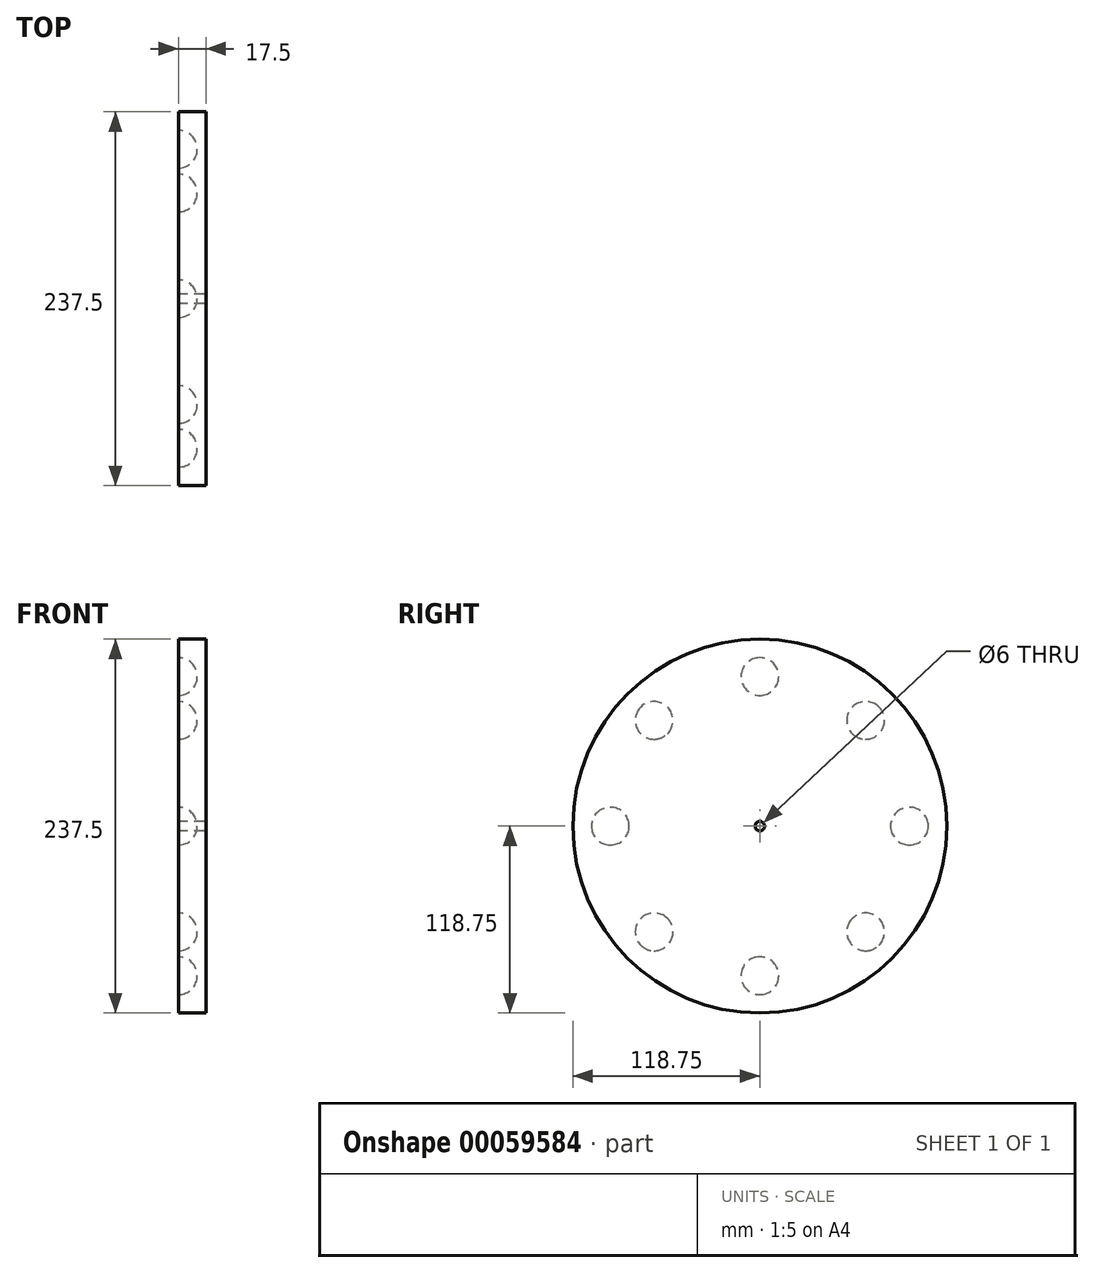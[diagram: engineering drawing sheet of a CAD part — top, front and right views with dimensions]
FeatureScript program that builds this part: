
annotation { "Feature Type Name" : "Feature", "Feature Type Description" : "" }
export const myFeature = defineFeature(function(context is Context, id is Id, definition is map)
    precondition{}
    {
        {
            var Q0;
            Q0=qCreatedBy(makeId("Right.planeOp"),FACE);
            var sketch = newSketch(context, id + "F0", { "sketchPlane" : qUnion([Q0])});
            skCircle(sketch, "E0", {"center": v(0, 0) * mm, "radius": 125 * mm, "construction": true});
            skCircle(sketch, "E1", {"center": v(0, 0) * mm, "radius": 0.81 * mm, "construction": true});
            skLineSegment(sketch, "E2", {"start": v(0, -0.81) * mm, "end": v(0, 0) * mm, "construction": true});
            skLineSegment(sketch, "E3", {"start": v(0, 0.81) * mm, "end": v(0, -0.81) * mm});
            skLineSegment(sketch, "E4", {"start": v(0, -0.81) * mm, "end": v(-5.3, 118.63) * mm});
            skLineSegment(sketch, "E5.MirrorCS", {"start": v(0, -0.81) * mm, "end": v(0, 0.81) * mm});
            skLineSegment(sketch, "E6.MirrorCS", {"start": v(0, -0.81) * mm, "end": v(5.3, 118.63) * mm});
            skCircle(sketch, "E7", {"center": v(0, 0) * mm, "radius": 118.75 * mm, "construction": true});
            skCircle(sketch, "E8", {"center": v(0, 0) * mm, "radius": 118.75 * mm});
            skLineSegment(sketch, "E9.1.0", {"start": v(0.1, -0.8) * mm, "end": v(-9.61, 118.36) * mm});
            skLineSegment(sketch, "E9.1.1", {"start": v(0.1, -0.8) * mm, "end": v(-20.13, 117.03) * mm});
            skLineSegment(sketch, "E9.1.2", {"start": v(-0.1, 0.8) * mm, "end": v(0.1, -0.8) * mm});
            skLineSegment(sketch, "E9.1.3", {"start": v(0.1, -0.8) * mm, "end": v(-0.1, 0.8) * mm});
            skLineSegment(sketch, "E9.2.0", {"start": v(0.2, -0.79) * mm, "end": v(-24.37, 116.22) * mm});
            skLineSegment(sketch, "E9.2.1", {"start": v(0.2, -0.79) * mm, "end": v(-34.64, 113.59) * mm});
            skLineSegment(sketch, "E9.2.2", {"start": v(-0.2, 0.79) * mm, "end": v(0.2, -0.79) * mm});
            skLineSegment(sketch, "E9.2.3", {"start": v(0.2, -0.79) * mm, "end": v(-0.2, 0.79) * mm});
            skLineSegment(sketch, "E10.3.3.0", {"start": v(0.3, -0.76) * mm, "end": v(-48.6, 108.35) * mm});
            skLineSegment(sketch, "E10.5.3.0", {"start": v(0.3, -0.76) * mm, "end": v(-38.74, 112.25) * mm});
            skLineSegment(sketch, "E10.6.3.0", {"start": v(-0.3, 0.76) * mm, "end": v(0.3, -0.76) * mm});
            skLineSegment(sketch, "E10.9.3.0", {"start": v(0.3, -0.76) * mm, "end": v(-0.3, 0.76) * mm});
            skLineSegment(sketch, "E10.3.4.0", {"start": v(0.4, -0.71) * mm, "end": v(-61.8, 101.4) * mm});
            skLineSegment(sketch, "E10.5.4.0", {"start": v(0.4, -0.71) * mm, "end": v(-52.5, 106.51) * mm});
            skLineSegment(sketch, "E10.6.4.0", {"start": v(-0.4, 0.71) * mm, "end": v(0.4, -0.71) * mm});
            skLineSegment(sketch, "E10.9.4.0", {"start": v(0.4, -0.71) * mm, "end": v(-0.4, 0.71) * mm});
            skLineSegment(sketch, "E10.3.5.0", {"start": v(0.48, -0.66) * mm, "end": v(-74.02, 92.86) * mm});
            skLineSegment(sketch, "E10.5.5.0", {"start": v(0.48, -0.66) * mm, "end": v(-65.44, 99.1) * mm});
            skLineSegment(sketch, "E10.6.5.0", {"start": v(-0.48, 0.66) * mm, "end": v(0.48, -0.66) * mm});
            skLineSegment(sketch, "E10.9.5.0", {"start": v(0.48, -0.66) * mm, "end": v(-0.48, 0.66) * mm});
            skLineSegment(sketch, "E10.3.6.0", {"start": v(0.56, -0.6) * mm, "end": v(-85.07, 82.85) * mm});
            skLineSegment(sketch, "E10.5.6.0", {"start": v(0.56, -0.6) * mm, "end": v(-77.35, 90.1) * mm});
            skLineSegment(sketch, "E10.6.6.0", {"start": v(-0.56, 0.6) * mm, "end": v(0.56, -0.6) * mm});
            skLineSegment(sketch, "E10.9.6.0", {"start": v(0.56, -0.6) * mm, "end": v(-0.56, 0.6) * mm});
            skLineSegment(sketch, "E10.3.7.0", {"start": v(0.63, -0.52) * mm, "end": v(-94.79, 71.53) * mm});
            skLineSegment(sketch, "E10.5.7.0", {"start": v(0.63, -0.52) * mm, "end": v(-88.03, 79.7) * mm});
            skLineSegment(sketch, "E10.6.7.0", {"start": v(-0.63, 0.52) * mm, "end": v(0.63, -0.52) * mm});
            skLineSegment(sketch, "E10.9.7.0", {"start": v(0.63, -0.52) * mm, "end": v(-0.63, 0.52) * mm});
            skLineSegment(sketch, "E10.3.8.0", {"start": v(0.69, -0.44) * mm, "end": v(-103, 59.1) * mm});
            skLineSegment(sketch, "E10.5.8.0", {"start": v(0.69, -0.44) * mm, "end": v(-97.32, 68.04) * mm});
            skLineSegment(sketch, "E10.6.8.0", {"start": v(-0.69, 0.44) * mm, "end": v(0.69, -0.44) * mm});
            skLineSegment(sketch, "E10.9.8.0", {"start": v(0.69, -0.44) * mm, "end": v(-0.69, 0.44) * mm});
            skLineSegment(sketch, "E10.3.9.0", {"start": v(0.74, -0.35) * mm, "end": v(-109.6, 45.72) * mm});
            skLineSegment(sketch, "E10.5.9.0", {"start": v(0.74, -0.35) * mm, "end": v(-105.08, 55.3) * mm});
            skLineSegment(sketch, "E10.6.9.0", {"start": v(-0.74, 0.35) * mm, "end": v(0.74, -0.35) * mm});
            skLineSegment(sketch, "E10.9.9.0", {"start": v(0.74, -0.35) * mm, "end": v(-0.74, 0.35) * mm});
            skLineSegment(sketch, "E10.3.10.0", {"start": v(0.77, -0.25) * mm, "end": v(-114.46, 31.62) * mm});
            skLineSegment(sketch, "E10.5.10.0", {"start": v(0.77, -0.25) * mm, "end": v(-111.19, 41.7) * mm});
            skLineSegment(sketch, "E10.6.10.0", {"start": v(-0.77, 0.25) * mm, "end": v(0.77, -0.25) * mm});
            skLineSegment(sketch, "E10.9.10.0", {"start": v(0.77, -0.25) * mm, "end": v(-0.77, 0.25) * mm});
            skLineSegment(sketch, "E10.3.11.0", {"start": v(0.8, -0.15) * mm, "end": v(-117.52, 17.02) * mm});
            skLineSegment(sketch, "E10.5.11.0", {"start": v(0.8, -0.15) * mm, "end": v(-115.54, 27.44) * mm});
            skLineSegment(sketch, "E10.6.11.0", {"start": v(-0.8, 0.15) * mm, "end": v(0.8, -0.15) * mm});
            skLineSegment(sketch, "E10.9.11.0", {"start": v(0.8, -0.15) * mm, "end": v(-0.8, 0.15) * mm});
            skLineSegment(sketch, "E10.3.12.0", {"start": v(0.81, -0.05) * mm, "end": v(-118.73, 2.16) * mm});
            skLineSegment(sketch, "E10.5.12.0", {"start": v(0.81, -0.05) * mm, "end": v(-118.06, 12.74) * mm});
            skLineSegment(sketch, "E10.6.12.0", {"start": v(-0.81, 0.05) * mm, "end": v(0.81, -0.05) * mm});
            skLineSegment(sketch, "E10.9.12.0", {"start": v(0.81, -0.05) * mm, "end": v(-0.81, 0.05) * mm});
            skLineSegment(sketch, "E10.3.13.0", {"start": v(0.81, 0.05) * mm, "end": v(-118.06, -12.74) * mm});
            skLineSegment(sketch, "E10.5.13.0", {"start": v(0.81, 0.05) * mm, "end": v(-118.73, -2.16) * mm});
            skLineSegment(sketch, "E10.6.13.0", {"start": v(-0.81, -0.05) * mm, "end": v(0.81, 0.05) * mm});
            skLineSegment(sketch, "E10.9.13.0", {"start": v(0.81, 0.05) * mm, "end": v(-0.81, -0.05) * mm});
            skLineSegment(sketch, "E10.3.14.0", {"start": v(0.8, 0.15) * mm, "end": v(-115.54, -27.44) * mm});
            skLineSegment(sketch, "E10.5.14.0", {"start": v(0.8, 0.15) * mm, "end": v(-117.52, -17.02) * mm});
            skLineSegment(sketch, "E10.6.14.0", {"start": v(-0.8, -0.15) * mm, "end": v(0.8, 0.15) * mm});
            skLineSegment(sketch, "E10.9.14.0", {"start": v(0.8, 0.15) * mm, "end": v(-0.8, -0.15) * mm});
            skLineSegment(sketch, "E10.3.15.0", {"start": v(0.77, 0.25) * mm, "end": v(-111.19, -41.7) * mm});
            skLineSegment(sketch, "E10.5.15.0", {"start": v(0.77, 0.25) * mm, "end": v(-114.46, -31.62) * mm});
            skLineSegment(sketch, "E10.6.15.0", {"start": v(-0.77, -0.25) * mm, "end": v(0.77, 0.25) * mm});
            skLineSegment(sketch, "E10.9.15.0", {"start": v(0.77, 0.25) * mm, "end": v(-0.77, -0.25) * mm});
            skLineSegment(sketch, "E10.3.16.0", {"start": v(0.74, 0.35) * mm, "end": v(-105.08, -55.3) * mm});
            skLineSegment(sketch, "E10.5.16.0", {"start": v(0.74, 0.35) * mm, "end": v(-109.6, -45.72) * mm});
            skLineSegment(sketch, "E10.6.16.0", {"start": v(-0.74, -0.35) * mm, "end": v(0.74, 0.35) * mm});
            skLineSegment(sketch, "E10.9.16.0", {"start": v(0.74, 0.35) * mm, "end": v(-0.74, -0.35) * mm});
            skLineSegment(sketch, "E10.3.17.0", {"start": v(0.69, 0.44) * mm, "end": v(-97.32, -68.04) * mm});
            skLineSegment(sketch, "E10.5.17.0", {"start": v(0.69, 0.44) * mm, "end": v(-103, -59.1) * mm});
            skLineSegment(sketch, "E10.6.17.0", {"start": v(-0.69, -0.44) * mm, "end": v(0.69, 0.44) * mm});
            skLineSegment(sketch, "E10.9.17.0", {"start": v(0.69, 0.44) * mm, "end": v(-0.69, -0.44) * mm});
            skLineSegment(sketch, "E10.3.18.0", {"start": v(0.63, 0.52) * mm, "end": v(-88.03, -79.7) * mm});
            skLineSegment(sketch, "E10.5.18.0", {"start": v(0.63, 0.52) * mm, "end": v(-94.79, -71.53) * mm});
            skLineSegment(sketch, "E10.6.18.0", {"start": v(-0.63, -0.52) * mm, "end": v(0.63, 0.52) * mm});
            skLineSegment(sketch, "E10.9.18.0", {"start": v(0.63, 0.52) * mm, "end": v(-0.63, -0.52) * mm});
            skLineSegment(sketch, "E10.3.19.0", {"start": v(0.56, 0.6) * mm, "end": v(-77.35, -90.1) * mm});
            skLineSegment(sketch, "E10.5.19.0", {"start": v(0.56, 0.6) * mm, "end": v(-85.07, -82.85) * mm});
            skLineSegment(sketch, "E10.6.19.0", {"start": v(-0.56, -0.6) * mm, "end": v(0.56, 0.6) * mm});
            skLineSegment(sketch, "E10.9.19.0", {"start": v(0.56, 0.6) * mm, "end": v(-0.56, -0.6) * mm});
            skLineSegment(sketch, "E10.3.20.0", {"start": v(0.48, 0.66) * mm, "end": v(-65.44, -99.1) * mm});
            skLineSegment(sketch, "E10.5.20.0", {"start": v(0.48, 0.66) * mm, "end": v(-74.02, -92.86) * mm});
            skLineSegment(sketch, "E10.6.20.0", {"start": v(-0.48, -0.66) * mm, "end": v(0.48, 0.66) * mm});
            skLineSegment(sketch, "E10.9.20.0", {"start": v(0.48, 0.66) * mm, "end": v(-0.48, -0.66) * mm});
            skLineSegment(sketch, "E10.3.21.0", {"start": v(0.4, 0.71) * mm, "end": v(-52.5, -106.51) * mm});
            skLineSegment(sketch, "E10.5.21.0", {"start": v(0.4, 0.71) * mm, "end": v(-61.8, -101.4) * mm});
            skLineSegment(sketch, "E10.6.21.0", {"start": v(-0.4, -0.71) * mm, "end": v(0.4, 0.71) * mm});
            skLineSegment(sketch, "E10.9.21.0", {"start": v(0.4, 0.71) * mm, "end": v(-0.4, -0.71) * mm});
            skLineSegment(sketch, "E10.3.22.0", {"start": v(0.3, 0.76) * mm, "end": v(-38.74, -112.25) * mm});
            skLineSegment(sketch, "E10.5.22.0", {"start": v(0.3, 0.76) * mm, "end": v(-48.6, -108.35) * mm});
            skLineSegment(sketch, "E10.6.22.0", {"start": v(-0.3, -0.76) * mm, "end": v(0.3, 0.76) * mm});
            skLineSegment(sketch, "E10.9.22.0", {"start": v(0.3, 0.76) * mm, "end": v(-0.3, -0.76) * mm});
            skLineSegment(sketch, "E10.3.23.0", {"start": v(0.2, 0.79) * mm, "end": v(-24.37, -116.22) * mm});
            skLineSegment(sketch, "E10.5.23.0", {"start": v(0.2, 0.79) * mm, "end": v(-34.64, -113.59) * mm});
            skLineSegment(sketch, "E10.6.23.0", {"start": v(-0.2, -0.79) * mm, "end": v(0.2, 0.79) * mm});
            skLineSegment(sketch, "E10.9.23.0", {"start": v(0.2, 0.79) * mm, "end": v(-0.2, -0.79) * mm});
            skLineSegment(sketch, "E10.3.24.0", {"start": v(0.1, 0.8) * mm, "end": v(-9.61, -118.36) * mm});
            skLineSegment(sketch, "E10.5.24.0", {"start": v(0.1, 0.8) * mm, "end": v(-20.13, -117.03) * mm});
            skLineSegment(sketch, "E10.6.24.0", {"start": v(-0.1, -0.8) * mm, "end": v(0.1, 0.8) * mm});
            skLineSegment(sketch, "E10.9.24.0", {"start": v(0.1, 0.8) * mm, "end": v(-0.1, -0.8) * mm});
            skLineSegment(sketch, "E10.3.25.0", {"start": v(0, 0.81) * mm, "end": v(5.3, -118.63) * mm});
            skLineSegment(sketch, "E10.5.25.0", {"start": v(0, 0.81) * mm, "end": v(-5.3, -118.63) * mm});
            skLineSegment(sketch, "E10.3.26.0", {"start": v(-0.1, 0.8) * mm, "end": v(20.13, -117.03) * mm});
            skLineSegment(sketch, "E10.5.26.0", {"start": v(-0.1, 0.8) * mm, "end": v(9.61, -118.36) * mm});
            skLineSegment(sketch, "E10.3.27.0", {"start": v(-0.2, 0.79) * mm, "end": v(34.64, -113.59) * mm});
            skLineSegment(sketch, "E10.5.27.0", {"start": v(-0.2, 0.79) * mm, "end": v(24.37, -116.22) * mm});
            skLineSegment(sketch, "E10.3.28.0", {"start": v(-0.3, 0.76) * mm, "end": v(48.6, -108.35) * mm});
            skLineSegment(sketch, "E10.5.28.0", {"start": v(-0.3, 0.76) * mm, "end": v(38.74, -112.25) * mm});
            skLineSegment(sketch, "E10.6.28.0", {"start": v(0.3, -0.76) * mm, "end": v(-0.3, 0.76) * mm});
            skLineSegment(sketch, "E10.9.28.0", {"start": v(-0.3, 0.76) * mm, "end": v(0.3, -0.76) * mm});
            skLineSegment(sketch, "E10.3.29.0", {"start": v(-0.4, 0.71) * mm, "end": v(61.8, -101.4) * mm});
            skLineSegment(sketch, "E10.5.29.0", {"start": v(-0.4, 0.71) * mm, "end": v(52.5, -106.51) * mm});
            skLineSegment(sketch, "E10.6.29.0", {"start": v(0.4, -0.71) * mm, "end": v(-0.4, 0.71) * mm});
            skLineSegment(sketch, "E10.9.29.0", {"start": v(-0.4, 0.71) * mm, "end": v(0.4, -0.71) * mm});
            skLineSegment(sketch, "E10.3.30.0", {"start": v(-0.48, 0.66) * mm, "end": v(74.02, -92.86) * mm});
            skLineSegment(sketch, "E10.5.30.0", {"start": v(-0.48, 0.66) * mm, "end": v(65.44, -99.1) * mm});
            skLineSegment(sketch, "E10.6.30.0", {"start": v(0.48, -0.66) * mm, "end": v(-0.48, 0.66) * mm});
            skLineSegment(sketch, "E10.9.30.0", {"start": v(-0.48, 0.66) * mm, "end": v(0.48, -0.66) * mm});
            skLineSegment(sketch, "E10.3.31.0", {"start": v(-0.56, 0.6) * mm, "end": v(85.07, -82.85) * mm});
            skLineSegment(sketch, "E10.5.31.0", {"start": v(-0.56, 0.6) * mm, "end": v(77.35, -90.1) * mm});
            skLineSegment(sketch, "E10.6.31.0", {"start": v(0.56, -0.6) * mm, "end": v(-0.56, 0.6) * mm});
            skLineSegment(sketch, "E10.9.31.0", {"start": v(-0.56, 0.6) * mm, "end": v(0.56, -0.6) * mm});
            skLineSegment(sketch, "E10.3.32.0", {"start": v(-0.63, 0.52) * mm, "end": v(94.79, -71.53) * mm});
            skLineSegment(sketch, "E10.5.32.0", {"start": v(-0.63, 0.52) * mm, "end": v(88.03, -79.7) * mm});
            skLineSegment(sketch, "E10.6.32.0", {"start": v(0.63, -0.52) * mm, "end": v(-0.63, 0.52) * mm});
            skLineSegment(sketch, "E10.9.32.0", {"start": v(-0.63, 0.52) * mm, "end": v(0.63, -0.52) * mm});
            skLineSegment(sketch, "E10.3.33.0", {"start": v(-0.69, 0.44) * mm, "end": v(103, -59.1) * mm});
            skLineSegment(sketch, "E10.5.33.0", {"start": v(-0.69, 0.44) * mm, "end": v(97.32, -68.04) * mm});
            skLineSegment(sketch, "E10.6.33.0", {"start": v(0.69, -0.44) * mm, "end": v(-0.69, 0.44) * mm});
            skLineSegment(sketch, "E10.9.33.0", {"start": v(-0.69, 0.44) * mm, "end": v(0.69, -0.44) * mm});
            skLineSegment(sketch, "E10.3.34.0", {"start": v(-0.74, 0.35) * mm, "end": v(109.6, -45.72) * mm});
            skLineSegment(sketch, "E10.5.34.0", {"start": v(-0.74, 0.35) * mm, "end": v(105.08, -55.3) * mm});
            skLineSegment(sketch, "E10.6.34.0", {"start": v(0.74, -0.35) * mm, "end": v(-0.74, 0.35) * mm});
            skLineSegment(sketch, "E10.9.34.0", {"start": v(-0.74, 0.35) * mm, "end": v(0.74, -0.35) * mm});
            skLineSegment(sketch, "E10.3.35.0", {"start": v(-0.77, 0.25) * mm, "end": v(114.46, -31.62) * mm});
            skLineSegment(sketch, "E10.5.35.0", {"start": v(-0.77, 0.25) * mm, "end": v(111.19, -41.7) * mm});
            skLineSegment(sketch, "E10.6.35.0", {"start": v(0.77, -0.25) * mm, "end": v(-0.77, 0.25) * mm});
            skLineSegment(sketch, "E10.9.35.0", {"start": v(-0.77, 0.25) * mm, "end": v(0.77, -0.25) * mm});
            skLineSegment(sketch, "E10.3.36.0", {"start": v(-0.8, 0.15) * mm, "end": v(117.52, -17.02) * mm});
            skLineSegment(sketch, "E10.5.36.0", {"start": v(-0.8, 0.15) * mm, "end": v(115.54, -27.44) * mm});
            skLineSegment(sketch, "E10.6.36.0", {"start": v(0.8, -0.15) * mm, "end": v(-0.8, 0.15) * mm});
            skLineSegment(sketch, "E10.9.36.0", {"start": v(-0.8, 0.15) * mm, "end": v(0.8, -0.15) * mm});
            skLineSegment(sketch, "E10.3.37.0", {"start": v(-0.81, 0.05) * mm, "end": v(118.73, -2.16) * mm});
            skLineSegment(sketch, "E10.5.37.0", {"start": v(-0.81, 0.05) * mm, "end": v(118.06, -12.74) * mm});
            skLineSegment(sketch, "E10.6.37.0", {"start": v(0.81, -0.05) * mm, "end": v(-0.81, 0.05) * mm});
            skLineSegment(sketch, "E10.9.37.0", {"start": v(-0.81, 0.05) * mm, "end": v(0.81, -0.05) * mm});
            skLineSegment(sketch, "E10.3.38.0", {"start": v(-0.81, -0.05) * mm, "end": v(118.06, 12.74) * mm});
            skLineSegment(sketch, "E10.5.38.0", {"start": v(-0.81, -0.05) * mm, "end": v(118.73, 2.16) * mm});
            skLineSegment(sketch, "E10.6.38.0", {"start": v(0.81, 0.05) * mm, "end": v(-0.81, -0.05) * mm});
            skLineSegment(sketch, "E10.9.38.0", {"start": v(-0.81, -0.05) * mm, "end": v(0.81, 0.05) * mm});
            skLineSegment(sketch, "E10.3.39.0", {"start": v(-0.8, -0.15) * mm, "end": v(115.54, 27.44) * mm});
            skLineSegment(sketch, "E10.5.39.0", {"start": v(-0.8, -0.15) * mm, "end": v(117.52, 17.02) * mm});
            skLineSegment(sketch, "E10.6.39.0", {"start": v(0.8, 0.15) * mm, "end": v(-0.8, -0.15) * mm});
            skLineSegment(sketch, "E10.9.39.0", {"start": v(-0.8, -0.15) * mm, "end": v(0.8, 0.15) * mm});
            skLineSegment(sketch, "E10.3.40.0", {"start": v(-0.77, -0.25) * mm, "end": v(111.19, 41.7) * mm});
            skLineSegment(sketch, "E10.5.40.0", {"start": v(-0.77, -0.25) * mm, "end": v(114.46, 31.62) * mm});
            skLineSegment(sketch, "E10.6.40.0", {"start": v(0.77, 0.25) * mm, "end": v(-0.77, -0.25) * mm});
            skLineSegment(sketch, "E10.9.40.0", {"start": v(-0.77, -0.25) * mm, "end": v(0.77, 0.25) * mm});
            skLineSegment(sketch, "E10.3.41.0", {"start": v(-0.74, -0.35) * mm, "end": v(105.08, 55.3) * mm});
            skLineSegment(sketch, "E10.5.41.0", {"start": v(-0.74, -0.35) * mm, "end": v(109.6, 45.72) * mm});
            skLineSegment(sketch, "E10.6.41.0", {"start": v(0.74, 0.35) * mm, "end": v(-0.74, -0.35) * mm});
            skLineSegment(sketch, "E10.9.41.0", {"start": v(-0.74, -0.35) * mm, "end": v(0.74, 0.35) * mm});
            skLineSegment(sketch, "E10.3.42.0", {"start": v(-0.69, -0.44) * mm, "end": v(97.32, 68.04) * mm});
            skLineSegment(sketch, "E10.5.42.0", {"start": v(-0.69, -0.44) * mm, "end": v(103, 59.1) * mm});
            skLineSegment(sketch, "E10.6.42.0", {"start": v(0.69, 0.44) * mm, "end": v(-0.69, -0.44) * mm});
            skLineSegment(sketch, "E10.9.42.0", {"start": v(-0.69, -0.44) * mm, "end": v(0.69, 0.44) * mm});
            skLineSegment(sketch, "E10.3.43.0", {"start": v(-0.63, -0.52) * mm, "end": v(88.03, 79.7) * mm});
            skLineSegment(sketch, "E10.5.43.0", {"start": v(-0.63, -0.52) * mm, "end": v(94.79, 71.53) * mm});
            skLineSegment(sketch, "E10.6.43.0", {"start": v(0.63, 0.52) * mm, "end": v(-0.63, -0.52) * mm});
            skLineSegment(sketch, "E10.9.43.0", {"start": v(-0.63, -0.52) * mm, "end": v(0.63, 0.52) * mm});
            skLineSegment(sketch, "E10.3.44.0", {"start": v(-0.56, -0.6) * mm, "end": v(77.35, 90.1) * mm});
            skLineSegment(sketch, "E10.5.44.0", {"start": v(-0.56, -0.6) * mm, "end": v(85.07, 82.85) * mm});
            skLineSegment(sketch, "E10.6.44.0", {"start": v(0.56, 0.6) * mm, "end": v(-0.56, -0.6) * mm});
            skLineSegment(sketch, "E10.9.44.0", {"start": v(-0.56, -0.6) * mm, "end": v(0.56, 0.6) * mm});
            skLineSegment(sketch, "E10.3.45.0", {"start": v(-0.48, -0.66) * mm, "end": v(65.44, 99.1) * mm});
            skLineSegment(sketch, "E10.5.45.0", {"start": v(-0.48, -0.66) * mm, "end": v(74.02, 92.86) * mm});
            skLineSegment(sketch, "E10.6.45.0", {"start": v(0.48, 0.66) * mm, "end": v(-0.48, -0.66) * mm});
            skLineSegment(sketch, "E10.9.45.0", {"start": v(-0.48, -0.66) * mm, "end": v(0.48, 0.66) * mm});
            skLineSegment(sketch, "E10.3.46.0", {"start": v(-0.4, -0.71) * mm, "end": v(52.5, 106.51) * mm});
            skLineSegment(sketch, "E10.5.46.0", {"start": v(-0.4, -0.71) * mm, "end": v(61.8, 101.4) * mm});
            skLineSegment(sketch, "E10.6.46.0", {"start": v(0.4, 0.71) * mm, "end": v(-0.4, -0.71) * mm});
            skLineSegment(sketch, "E10.9.46.0", {"start": v(-0.4, -0.71) * mm, "end": v(0.4, 0.71) * mm});
            skLineSegment(sketch, "E10.3.47.0", {"start": v(-0.3, -0.76) * mm, "end": v(38.74, 112.25) * mm});
            skLineSegment(sketch, "E10.5.47.0", {"start": v(-0.3, -0.76) * mm, "end": v(48.6, 108.35) * mm});
            skLineSegment(sketch, "E10.6.47.0", {"start": v(0.3, 0.76) * mm, "end": v(-0.3, -0.76) * mm});
            skLineSegment(sketch, "E10.9.47.0", {"start": v(-0.3, -0.76) * mm, "end": v(0.3, 0.76) * mm});
            skLineSegment(sketch, "E10.3.48.0", {"start": v(-0.2, -0.79) * mm, "end": v(24.37, 116.22) * mm});
            skLineSegment(sketch, "E10.5.48.0", {"start": v(-0.2, -0.79) * mm, "end": v(34.64, 113.59) * mm});
            skLineSegment(sketch, "E10.6.48.0", {"start": v(0.2, 0.79) * mm, "end": v(-0.2, -0.79) * mm});
            skLineSegment(sketch, "E10.9.48.0", {"start": v(-0.2, -0.79) * mm, "end": v(0.2, 0.79) * mm});
            skLineSegment(sketch, "E10.3.49.0", {"start": v(-0.1, -0.8) * mm, "end": v(9.61, 118.36) * mm});
            skLineSegment(sketch, "E10.5.49.0", {"start": v(-0.1, -0.8) * mm, "end": v(20.13, 117.03) * mm});
            skLineSegment(sketch, "E10.6.49.0", {"start": v(0.1, 0.8) * mm, "end": v(-0.1, -0.8) * mm});
            skLineSegment(sketch, "E10.9.49.0", {"start": v(-0.1, -0.8) * mm, "end": v(0.1, 0.8) * mm});
            skSolve(sketch);
        }
        {
            var Q0;
            Q0 = qSketchRegion(id + "F0", true);
            extrude(context, id + "F1", {"entities" : qUnion([Q0]), "depth" : 17.5 * mm});
        }
        {
            var Q0;
            Q0=makeQuery(id+"Fn8MloqXUjJoPmc_1.boolean.opBoolean","MERGE",FACE,{"derivedFrom":[makeQuery(id+"F1.opExtrude","CAP_FACE",FACE,{"disambiguationData":[OSD([sQuery(id+"F0.wireOp",EDGE,"E3"),sQuery(id+"F0.wireOp",EDGE,"E4"),sQuery(id+"F0.wireOp",EDGE,"E5.MirrorCS"),sQuery(id+"F0.wireOp",EDGE,"E6.MirrorCS"),sQuery(id+"F0.wireOp",EDGE,"OQRqwsvV-qcOx-RosJ-7bpL-tB40Y6nJSxaw"),sQuery(id+"F0.wireOp",EDGE,"t5HJLBER-EOSb-2UTf-ySmI-mLM6b4EdJLG6"),sQuery(id+"F0.wireOp",EDGE,"OaBUUnl9-dybp-6rTC-3uGv-TSD4vVyGhlnP")])],"isStart":true}),makeQuery(id+"Fn8MloqXUjJoPmc_1.opExtrude","CAP_FACE",FACE,{"disambiguationData":[OSD([sQuery(id+"Fj8ZmPuuntyTscv_1.wireOp",EDGE,"wY98nEZC-u4MA-k90t-BY2E-VeJdUgsrrei2")])],"isStart":true})]});
            var sketch = newSketch(context, id + "F2", { "sketchPlane" : qUnion([Q0])});
            skArc(sketch, "E11", {"start": v(0, 83) * mm, "mid": v(12, 95) * mm, "end": v(0, 107) * mm});
            skLineSegment(sketch, "E12", {"start": v(0, 83) * mm, "end": v(0, 107) * mm});
            skSolve(sketch);
        }
        {
            var Q0;
            Q0 = qSketchRegion(id + "F2", true);
            var Q1;
            Q1=sQuery(id+"F2.wireOp",EDGE,"E12");
            revolve(context, id + "F3", {"operationType" : NewBodyOperationType.REMOVE, "entities" : qUnion([Q0]), "axis" : qUnion([Q1]), "revolveType" : RevolveType.ONE_DIRECTION, "angle" : 180 * degree});
        }
        {
            var Q0;
            Q0=makeQuery(id+"Fn8MloqXUjJoPmc_1.boolean.opBoolean","MERGE",FACE,{"derivedFrom":[makeQuery(id+"F1.opExtrude","CAP_FACE",FACE,{"disambiguationData":[OSD([sQuery(id+"F0.wireOp",EDGE,"E3"),sQuery(id+"F0.wireOp",EDGE,"E4"),sQuery(id+"F0.wireOp",EDGE,"E5.MirrorCS"),sQuery(id+"F0.wireOp",EDGE,"E6.MirrorCS"),sQuery(id+"F0.wireOp",EDGE,"OQRqwsvV-qcOx-RosJ-7bpL-tB40Y6nJSxaw"),sQuery(id+"F0.wireOp",EDGE,"t5HJLBER-EOSb-2UTf-ySmI-mLM6b4EdJLG6"),sQuery(id+"F0.wireOp",EDGE,"OaBUUnl9-dybp-6rTC-3uGv-TSD4vVyGhlnP")])],"isStart":true}),makeQuery(id+"Fn8MloqXUjJoPmc_1.opExtrude","CAP_FACE",FACE,{"disambiguationData":[OSD([sQuery(id+"Fj8ZmPuuntyTscv_1.wireOp",EDGE,"wY98nEZC-u4MA-k90t-BY2E-VeJdUgsrrei2")])],"isStart":true})]});
            var sketch = newSketch(context, id + "F4", { "sketchPlane" : qUnion([Q0])});
            skArc(sketch, "E13", {"start": v(58.69, 58.69) * mm, "mid": v(75.66, 58.69) * mm, "end": v(75.66, 75.66) * mm});
            skLineSegment(sketch, "E14", {"start": v(0, 0) * mm, "end": v(67.18, 67.18) * mm, "construction": true});
            skLineSegment(sketch, "E15", {"start": v(58.69, 58.69) * mm, "end": v(75.66, 75.66) * mm});
            skSolve(sketch);
        }
        {
            var Q0;
            Q0=makeQuery(id+"F4.imprint","IMPRINT",FACE,{"disambiguationData":[TD([[makeQuery(id+"F4.imprint","IMPRINT",EDGE,{"derivedFrom":sQuery(id+"F4.wireOp",EDGE,"E13")}),1.0]])]});
            var Q1;
            Q1=sQuery(id+"F4.wireOp",EDGE,"E14");
            revolve(context, id + "F5", {"operationType" : NewBodyOperationType.REMOVE, "entities" : qUnion([Q0]), "axis" : qUnion([Q1]), "revolveType" : RevolveType.FULL, "oppositeDirection" : true});
        }
        {
            var Q0;
            Q0=makeQuery(id+"Fn8MloqXUjJoPmc_1.boolean.opBoolean","MERGE",FACE,{"derivedFrom":[makeQuery(id+"F1.opExtrude","CAP_FACE",FACE,{"disambiguationData":[OSD([sQuery(id+"F0.wireOp",EDGE,"E3"),sQuery(id+"F0.wireOp",EDGE,"E4"),sQuery(id+"F0.wireOp",EDGE,"E5.MirrorCS"),sQuery(id+"F0.wireOp",EDGE,"E6.MirrorCS"),sQuery(id+"F0.wireOp",EDGE,"OQRqwsvV-qcOx-RosJ-7bpL-tB40Y6nJSxaw"),sQuery(id+"F0.wireOp",EDGE,"t5HJLBER-EOSb-2UTf-ySmI-mLM6b4EdJLG6"),sQuery(id+"F0.wireOp",EDGE,"OaBUUnl9-dybp-6rTC-3uGv-TSD4vVyGhlnP")])],"isStart":true}),makeQuery(id+"Fn8MloqXUjJoPmc_1.opExtrude","CAP_FACE",FACE,{"disambiguationData":[OSD([sQuery(id+"Fj8ZmPuuntyTscv_1.wireOp",EDGE,"wY98nEZC-u4MA-k90t-BY2E-VeJdUgsrrei2")])],"isStart":true})]});
            var sketch = newSketch(context, id + "F6", { "sketchPlane" : qUnion([Q0])});
            skLineSegment(sketch, "E16", {"start": v(0, 0) * mm, "end": v(95, 0) * mm, "construction": true});
            skArc(sketch, "E17", {"start": v(83, 0) * mm, "mid": v(95, -12) * mm, "end": v(107, 0) * mm});
            skLineSegment(sketch, "E18", {"start": v(83, 0) * mm, "end": v(107, 0) * mm});
            skSolve(sketch);
        }
        {
            var Q0;
            Q0 = qSketchRegion(id + "F6", true);
            var Q1;
            Q1=sQuery(id+"F6.wireOp",EDGE,"E16");
            revolve(context, id + "F7", {"operationType" : NewBodyOperationType.REMOVE, "entities" : qUnion([Q0]), "axis" : qUnion([Q1]), "revolveType" : RevolveType.FULL, "oppositeDirection" : true});
        }
        {
            var Q0;
            Q0=makeQuery(id+"Fn8MloqXUjJoPmc_1.boolean.opBoolean","MERGE",FACE,{"derivedFrom":[makeQuery(id+"F1.opExtrude","CAP_FACE",FACE,{"disambiguationData":[OSD([sQuery(id+"F0.wireOp",EDGE,"E3"),sQuery(id+"F0.wireOp",EDGE,"E4"),sQuery(id+"F0.wireOp",EDGE,"E5.MirrorCS"),sQuery(id+"F0.wireOp",EDGE,"E6.MirrorCS"),sQuery(id+"F0.wireOp",EDGE,"OQRqwsvV-qcOx-RosJ-7bpL-tB40Y6nJSxaw"),sQuery(id+"F0.wireOp",EDGE,"t5HJLBER-EOSb-2UTf-ySmI-mLM6b4EdJLG6"),sQuery(id+"F0.wireOp",EDGE,"OaBUUnl9-dybp-6rTC-3uGv-TSD4vVyGhlnP")])],"isStart":true}),makeQuery(id+"Fn8MloqXUjJoPmc_1.opExtrude","CAP_FACE",FACE,{"disambiguationData":[OSD([sQuery(id+"Fj8ZmPuuntyTscv_1.wireOp",EDGE,"wY98nEZC-u4MA-k90t-BY2E-VeJdUgsrrei2")])],"isStart":true})]});
            var sketch = newSketch(context, id + "F8", { "sketchPlane" : qUnion([Q0])});
            skLineSegment(sketch, "E19", {"start": v(0, 0) * mm, "end": v(67.18, -67.18) * mm, "construction": true});
            skArc(sketch, "E20", {"start": v(58.69, -58.69) * mm, "mid": v(58.69, -75.66) * mm, "end": v(75.66, -75.66) * mm});
            skLineSegment(sketch, "E21", {"start": v(58.69, -58.69) * mm, "end": v(75.66, -75.66) * mm});
            skSolve(sketch);
        }
        {
            var Q0;
            Q0 = qSketchRegion(id + "F8", true);
            var Q1;
            Q1=sQuery(id+"F8.wireOp",EDGE,"E21");
            revolve(context, id + "F9", {"operationType" : NewBodyOperationType.REMOVE, "entities" : qUnion([Q0]), "axis" : qUnion([Q1]), "revolveType" : RevolveType.FULL, "oppositeDirection" : true});
        }
        {
            var Q0;
            Q0=makeQuery(id+"Fn8MloqXUjJoPmc_1.boolean.opBoolean","MERGE",FACE,{"derivedFrom":[makeQuery(id+"F1.opExtrude","CAP_FACE",FACE,{"disambiguationData":[OSD([sQuery(id+"F0.wireOp",EDGE,"E3"),sQuery(id+"F0.wireOp",EDGE,"E4"),sQuery(id+"F0.wireOp",EDGE,"E5.MirrorCS"),sQuery(id+"F0.wireOp",EDGE,"E6.MirrorCS"),sQuery(id+"F0.wireOp",EDGE,"OQRqwsvV-qcOx-RosJ-7bpL-tB40Y6nJSxaw"),sQuery(id+"F0.wireOp",EDGE,"t5HJLBER-EOSb-2UTf-ySmI-mLM6b4EdJLG6"),sQuery(id+"F0.wireOp",EDGE,"OaBUUnl9-dybp-6rTC-3uGv-TSD4vVyGhlnP")])],"isStart":true}),makeQuery(id+"Fn8MloqXUjJoPmc_1.opExtrude","CAP_FACE",FACE,{"disambiguationData":[OSD([sQuery(id+"Fj8ZmPuuntyTscv_1.wireOp",EDGE,"wY98nEZC-u4MA-k90t-BY2E-VeJdUgsrrei2")])],"isStart":true})]});
            var sketch = newSketch(context, id + "F10", { "sketchPlane" : qUnion([Q0])});
            skLineSegment(sketch, "E22", {"start": v(0, 0) * mm, "end": v(0, -95) * mm, "construction": true});
            skArc(sketch, "E23", {"start": v(0, -83) * mm, "mid": v(-12, -95) * mm, "end": v(0, -107) * mm});
            skLineSegment(sketch, "E24", {"start": v(0, -83) * mm, "end": v(0, -107) * mm});
            skSolve(sketch);
        }
        {
            var Q0;
            Q0 = qSketchRegion(id + "F10", true);
            var Q1;
            Q1=sQuery(id+"F10.wireOp",EDGE,"E24");
            revolve(context, id + "F11", {"operationType" : NewBodyOperationType.REMOVE, "entities" : qUnion([Q0]), "axis" : qUnion([Q1]), "revolveType" : RevolveType.FULL});
        }
        {
            var Q0;
            Q0=makeQuery(id+"Fn8MloqXUjJoPmc_1.boolean.opBoolean","MERGE",FACE,{"derivedFrom":[makeQuery(id+"F1.opExtrude","CAP_FACE",FACE,{"disambiguationData":[OSD([sQuery(id+"F0.wireOp",EDGE,"E3"),sQuery(id+"F0.wireOp",EDGE,"E4"),sQuery(id+"F0.wireOp",EDGE,"E5.MirrorCS"),sQuery(id+"F0.wireOp",EDGE,"E6.MirrorCS"),sQuery(id+"F0.wireOp",EDGE,"OQRqwsvV-qcOx-RosJ-7bpL-tB40Y6nJSxaw"),sQuery(id+"F0.wireOp",EDGE,"t5HJLBER-EOSb-2UTf-ySmI-mLM6b4EdJLG6"),sQuery(id+"F0.wireOp",EDGE,"OaBUUnl9-dybp-6rTC-3uGv-TSD4vVyGhlnP")])],"isStart":true}),makeQuery(id+"Fn8MloqXUjJoPmc_1.opExtrude","CAP_FACE",FACE,{"disambiguationData":[OSD([sQuery(id+"Fj8ZmPuuntyTscv_1.wireOp",EDGE,"wY98nEZC-u4MA-k90t-BY2E-VeJdUgsrrei2")])],"isStart":true})]});
            var sketch = newSketch(context, id + "F12", { "sketchPlane" : qUnion([Q0])});
            skLineSegment(sketch, "E25", {"start": v(0, 0) * mm, "end": v(-67.18, -67.18) * mm, "construction": true});
            skArc(sketch, "E26", {"start": v(-58.69, -58.69) * mm, "mid": v(-75.66, -58.69) * mm, "end": v(-75.66, -75.66) * mm});
            skLineSegment(sketch, "E27", {"start": v(-58.69, -58.69) * mm, "end": v(-75.66, -75.66) * mm});
            skSolve(sketch);
        }
        {
            var Q0;
            Q0=makeQuery(id+"F12.imprint","IMPRINT",FACE,{"disambiguationData":[TD([[makeQuery(id+"F12.imprint","IMPRINT",EDGE,{"derivedFrom":sQuery(id+"F12.wireOp",EDGE,"E26")}),1.0]])]});
            var Q1;
            Q1=sQuery(id+"F12.wireOp",EDGE,"E27");
            revolve(context, id + "F13", {"operationType" : NewBodyOperationType.REMOVE, "entities" : qUnion([Q0]), "axis" : qUnion([Q1]), "revolveType" : RevolveType.FULL, "oppositeDirection" : true});
        }
        {
            var Q0;
            Q0=makeQuery(id+"F1.opExtrude","CAP_FACE",FACE,{"disambiguationData":[OSD([sQuery(id+"F0.wireOp",EDGE,"E3"),sQuery(id+"F0.wireOp",EDGE,"E4"),sQuery(id+"F0.wireOp",EDGE,"E5.MirrorCS"),sQuery(id+"F0.wireOp",EDGE,"E6.MirrorCS"),sQuery(id+"F0.wireOp",EDGE,"E8"),sQuery(id+"F0.wireOp",EDGE,"E9.1.0"),sQuery(id+"F0.wireOp",EDGE,"E9.1.1"),sQuery(id+"F0.wireOp",EDGE,"E9.1.2"),sQuery(id+"F0.wireOp",EDGE,"E9.1.3"),sQuery(id+"F0.wireOp",EDGE,"E9.2.0"),sQuery(id+"F0.wireOp",EDGE,"E9.2.1"),sQuery(id+"F0.wireOp",EDGE,"E9.2.2"),sQuery(id+"F0.wireOp",EDGE,"E9.2.3"),sQuery(id+"F0.wireOp",EDGE,"E10.3.3.0"),sQuery(id+"F0.wireOp",EDGE,"E10.5.3.0"),sQuery(id+"F0.wireOp",EDGE,"E10.6.3.0"),sQuery(id+"F0.wireOp",EDGE,"E10.9.3.0"),sQuery(id+"F0.wireOp",EDGE,"E10.3.4.0"),sQuery(id+"F0.wireOp",EDGE,"E10.5.4.0"),sQuery(id+"F0.wireOp",EDGE,"E10.6.4.0"),sQuery(id+"F0.wireOp",EDGE,"E10.9.4.0"),sQuery(id+"F0.wireOp",EDGE,"E10.3.5.0"),sQuery(id+"F0.wireOp",EDGE,"E10.5.5.0"),sQuery(id+"F0.wireOp",EDGE,"E10.6.5.0"),sQuery(id+"F0.wireOp",EDGE,"E10.9.5.0"),sQuery(id+"F0.wireOp",EDGE,"E10.3.6.0"),sQuery(id+"F0.wireOp",EDGE,"E10.5.6.0"),sQuery(id+"F0.wireOp",EDGE,"E10.6.6.0"),sQuery(id+"F0.wireOp",EDGE,"E10.9.6.0"),sQuery(id+"F0.wireOp",EDGE,"E10.3.7.0"),sQuery(id+"F0.wireOp",EDGE,"E10.5.7.0"),sQuery(id+"F0.wireOp",EDGE,"E10.6.7.0"),sQuery(id+"F0.wireOp",EDGE,"E10.9.7.0"),sQuery(id+"F0.wireOp",EDGE,"E10.3.8.0"),sQuery(id+"F0.wireOp",EDGE,"E10.5.8.0"),sQuery(id+"F0.wireOp",EDGE,"E10.6.8.0"),sQuery(id+"F0.wireOp",EDGE,"E10.9.8.0"),sQuery(id+"F0.wireOp",EDGE,"E10.3.9.0"),sQuery(id+"F0.wireOp",EDGE,"E10.5.9.0"),sQuery(id+"F0.wireOp",EDGE,"E10.6.9.0"),sQuery(id+"F0.wireOp",EDGE,"E10.9.9.0"),sQuery(id+"F0.wireOp",EDGE,"E10.3.10.0"),sQuery(id+"F0.wireOp",EDGE,"E10.5.10.0"),sQuery(id+"F0.wireOp",EDGE,"E10.6.10.0"),sQuery(id+"F0.wireOp",EDGE,"E10.9.10.0"),sQuery(id+"F0.wireOp",EDGE,"E10.3.11.0"),sQuery(id+"F0.wireOp",EDGE,"E10.5.11.0"),sQuery(id+"F0.wireOp",EDGE,"E10.6.11.0"),sQuery(id+"F0.wireOp",EDGE,"E10.9.11.0"),sQuery(id+"F0.wireOp",EDGE,"E10.3.12.0"),sQuery(id+"F0.wireOp",EDGE,"E10.5.12.0"),sQuery(id+"F0.wireOp",EDGE,"E10.6.12.0"),sQuery(id+"F0.wireOp",EDGE,"E10.9.12.0"),sQuery(id+"F0.wireOp",EDGE,"E10.3.13.0"),sQuery(id+"F0.wireOp",EDGE,"E10.5.13.0"),sQuery(id+"F0.wireOp",EDGE,"E10.6.13.0"),sQuery(id+"F0.wireOp",EDGE,"E10.9.13.0"),sQuery(id+"F0.wireOp",EDGE,"E10.3.14.0"),sQuery(id+"F0.wireOp",EDGE,"E10.5.14.0"),sQuery(id+"F0.wireOp",EDGE,"E10.6.14.0"),sQuery(id+"F0.wireOp",EDGE,"E10.9.14.0"),sQuery(id+"F0.wireOp",EDGE,"E10.3.15.0"),sQuery(id+"F0.wireOp",EDGE,"E10.5.15.0"),sQuery(id+"F0.wireOp",EDGE,"E10.6.15.0"),sQuery(id+"F0.wireOp",EDGE,"E10.9.15.0"),sQuery(id+"F0.wireOp",EDGE,"E10.3.16.0"),sQuery(id+"F0.wireOp",EDGE,"E10.5.16.0"),sQuery(id+"F0.wireOp",EDGE,"E10.6.16.0"),sQuery(id+"F0.wireOp",EDGE,"E10.9.16.0"),sQuery(id+"F0.wireOp",EDGE,"E10.3.17.0"),sQuery(id+"F0.wireOp",EDGE,"E10.5.17.0"),sQuery(id+"F0.wireOp",EDGE,"E10.6.17.0"),sQuery(id+"F0.wireOp",EDGE,"E10.9.17.0"),sQuery(id+"F0.wireOp",EDGE,"E10.3.18.0"),sQuery(id+"F0.wireOp",EDGE,"E10.5.18.0"),sQuery(id+"F0.wireOp",EDGE,"E10.6.18.0"),sQuery(id+"F0.wireOp",EDGE,"E10.9.18.0"),sQuery(id+"F0.wireOp",EDGE,"E10.3.19.0"),sQuery(id+"F0.wireOp",EDGE,"E10.5.19.0"),sQuery(id+"F0.wireOp",EDGE,"E10.6.19.0"),sQuery(id+"F0.wireOp",EDGE,"E10.9.19.0"),sQuery(id+"F0.wireOp",EDGE,"E10.3.20.0"),sQuery(id+"F0.wireOp",EDGE,"E10.5.20.0"),sQuery(id+"F0.wireOp",EDGE,"E10.6.20.0"),sQuery(id+"F0.wireOp",EDGE,"E10.9.20.0"),sQuery(id+"F0.wireOp",EDGE,"E10.3.21.0"),sQuery(id+"F0.wireOp",EDGE,"E10.5.21.0"),sQuery(id+"F0.wireOp",EDGE,"E10.6.21.0"),sQuery(id+"F0.wireOp",EDGE,"E10.9.21.0"),sQuery(id+"F0.wireOp",EDGE,"E10.3.22.0"),sQuery(id+"F0.wireOp",EDGE,"E10.5.22.0"),sQuery(id+"F0.wireOp",EDGE,"E10.6.22.0"),sQuery(id+"F0.wireOp",EDGE,"E10.9.22.0"),sQuery(id+"F0.wireOp",EDGE,"E10.3.23.0"),sQuery(id+"F0.wireOp",EDGE,"E10.5.23.0"),sQuery(id+"F0.wireOp",EDGE,"E10.6.23.0"),sQuery(id+"F0.wireOp",EDGE,"E10.9.23.0"),sQuery(id+"F0.wireOp",EDGE,"E10.3.24.0"),sQuery(id+"F0.wireOp",EDGE,"E10.5.24.0"),sQuery(id+"F0.wireOp",EDGE,"E10.6.24.0"),sQuery(id+"F0.wireOp",EDGE,"E10.9.24.0"),sQuery(id+"F0.wireOp",EDGE,"E10.3.25.0"),sQuery(id+"F0.wireOp",EDGE,"E10.5.25.0"),sQuery(id+"F0.wireOp",EDGE,"E5.MirrorCS"),sQuery(id+"F0.wireOp",EDGE,"E3"),sQuery(id+"F0.wireOp",EDGE,"E10.3.26.0"),sQuery(id+"F0.wireOp",EDGE,"E10.5.26.0"),sQuery(id+"F0.wireOp",EDGE,"E9.1.3"),sQuery(id+"F0.wireOp",EDGE,"E9.1.2"),sQuery(id+"F0.wireOp",EDGE,"E10.3.27.0"),sQuery(id+"F0.wireOp",EDGE,"E10.5.27.0"),sQuery(id+"F0.wireOp",EDGE,"E9.2.3"),sQuery(id+"F0.wireOp",EDGE,"E9.2.2"),sQuery(id+"F0.wireOp",EDGE,"E10.3.28.0"),sQuery(id+"F0.wireOp",EDGE,"E10.5.28.0"),sQuery(id+"F0.wireOp",EDGE,"E10.6.28.0"),sQuery(id+"F0.wireOp",EDGE,"E10.9.28.0"),sQuery(id+"F0.wireOp",EDGE,"E10.3.29.0"),sQuery(id+"F0.wireOp",EDGE,"E10.5.29.0"),sQuery(id+"F0.wireOp",EDGE,"E10.6.29.0"),sQuery(id+"F0.wireOp",EDGE,"E10.9.29.0"),sQuery(id+"F0.wireOp",EDGE,"E10.3.30.0"),sQuery(id+"F0.wireOp",EDGE,"E10.5.30.0"),sQuery(id+"F0.wireOp",EDGE,"E10.6.30.0"),sQuery(id+"F0.wireOp",EDGE,"E10.9.30.0"),sQuery(id+"F0.wireOp",EDGE,"E10.3.31.0"),sQuery(id+"F0.wireOp",EDGE,"E10.5.31.0"),sQuery(id+"F0.wireOp",EDGE,"E10.6.31.0"),sQuery(id+"F0.wireOp",EDGE,"E10.9.31.0"),sQuery(id+"F0.wireOp",EDGE,"E10.3.32.0"),sQuery(id+"F0.wireOp",EDGE,"E10.5.32.0"),sQuery(id+"F0.wireOp",EDGE,"E10.6.32.0"),sQuery(id+"F0.wireOp",EDGE,"E10.9.32.0"),sQuery(id+"F0.wireOp",EDGE,"E10.3.33.0"),sQuery(id+"F0.wireOp",EDGE,"E10.5.33.0"),sQuery(id+"F0.wireOp",EDGE,"E10.6.33.0"),sQuery(id+"F0.wireOp",EDGE,"E10.9.33.0"),sQuery(id+"F0.wireOp",EDGE,"E10.3.34.0"),sQuery(id+"F0.wireOp",EDGE,"E10.5.34.0"),sQuery(id+"F0.wireOp",EDGE,"E10.6.34.0"),sQuery(id+"F0.wireOp",EDGE,"E10.9.34.0"),sQuery(id+"F0.wireOp",EDGE,"E10.3.35.0"),sQuery(id+"F0.wireOp",EDGE,"E10.5.35.0"),sQuery(id+"F0.wireOp",EDGE,"E10.6.35.0"),sQuery(id+"F0.wireOp",EDGE,"E10.9.35.0"),sQuery(id+"F0.wireOp",EDGE,"E10.3.36.0"),sQuery(id+"F0.wireOp",EDGE,"E10.5.36.0"),sQuery(id+"F0.wireOp",EDGE,"E10.6.36.0"),sQuery(id+"F0.wireOp",EDGE,"E10.9.36.0"),sQuery(id+"F0.wireOp",EDGE,"E10.3.37.0"),sQuery(id+"F0.wireOp",EDGE,"E10.5.37.0"),sQuery(id+"F0.wireOp",EDGE,"E10.6.37.0"),sQuery(id+"F0.wireOp",EDGE,"E10.9.37.0"),sQuery(id+"F0.wireOp",EDGE,"E10.3.38.0"),sQuery(id+"F0.wireOp",EDGE,"E10.5.38.0"),sQuery(id+"F0.wireOp",EDGE,"E10.6.38.0"),sQuery(id+"F0.wireOp",EDGE,"E10.9.38.0"),sQuery(id+"F0.wireOp",EDGE,"E10.3.39.0"),sQuery(id+"F0.wireOp",EDGE,"E10.5.39.0"),sQuery(id+"F0.wireOp",EDGE,"E10.6.39.0"),sQuery(id+"F0.wireOp",EDGE,"E10.9.39.0"),sQuery(id+"F0.wireOp",EDGE,"E10.3.40.0"),sQuery(id+"F0.wireOp",EDGE,"E10.5.40.0"),sQuery(id+"F0.wireOp",EDGE,"E10.6.40.0"),sQuery(id+"F0.wireOp",EDGE,"E10.9.40.0"),sQuery(id+"F0.wireOp",EDGE,"E10.3.41.0"),sQuery(id+"F0.wireOp",EDGE,"E10.5.41.0"),sQuery(id+"F0.wireOp",EDGE,"E10.6.41.0"),sQuery(id+"F0.wireOp",EDGE,"E10.9.41.0"),sQuery(id+"F0.wireOp",EDGE,"E10.3.42.0"),sQuery(id+"F0.wireOp",EDGE,"E10.5.42.0"),sQuery(id+"F0.wireOp",EDGE,"E10.6.42.0"),sQuery(id+"F0.wireOp",EDGE,"E10.9.42.0"),sQuery(id+"F0.wireOp",EDGE,"E10.3.43.0"),sQuery(id+"F0.wireOp",EDGE,"E10.5.43.0"),sQuery(id+"F0.wireOp",EDGE,"E10.6.43.0"),sQuery(id+"F0.wireOp",EDGE,"E10.9.43.0"),sQuery(id+"F0.wireOp",EDGE,"E10.3.44.0"),sQuery(id+"F0.wireOp",EDGE,"E10.5.44.0"),sQuery(id+"F0.wireOp",EDGE,"E10.6.44.0"),sQuery(id+"F0.wireOp",EDGE,"E10.9.44.0"),sQuery(id+"F0.wireOp",EDGE,"E10.3.45.0"),sQuery(id+"F0.wireOp",EDGE,"E10.5.45.0"),sQuery(id+"F0.wireOp",EDGE,"E10.6.45.0"),sQuery(id+"F0.wireOp",EDGE,"E10.9.45.0"),sQuery(id+"F0.wireOp",EDGE,"E10.3.46.0"),sQuery(id+"F0.wireOp",EDGE,"E10.5.46.0"),sQuery(id+"F0.wireOp",EDGE,"E10.6.46.0"),sQuery(id+"F0.wireOp",EDGE,"E10.9.46.0"),sQuery(id+"F0.wireOp",EDGE,"E10.3.47.0"),sQuery(id+"F0.wireOp",EDGE,"E10.5.47.0"),sQuery(id+"F0.wireOp",EDGE,"E10.6.47.0"),sQuery(id+"F0.wireOp",EDGE,"E10.9.47.0"),sQuery(id+"F0.wireOp",EDGE,"E10.3.48.0"),sQuery(id+"F0.wireOp",EDGE,"E10.5.48.0"),sQuery(id+"F0.wireOp",EDGE,"E10.6.48.0"),sQuery(id+"F0.wireOp",EDGE,"E10.9.48.0"),sQuery(id+"F0.wireOp",EDGE,"E10.3.49.0"),sQuery(id+"F0.wireOp",EDGE,"E10.5.49.0"),sQuery(id+"F0.wireOp",EDGE,"E10.6.49.0"),sQuery(id+"F0.wireOp",EDGE,"E10.9.49.0")])],"isStart":true});
            var sketch = newSketch(context, id + "F14", { "sketchPlane" : qUnion([Q0])});
            skLineSegment(sketch, "E28", {"start": v(0, 0) * mm, "end": v(-95, 0) * mm, "construction": true});
            skArc(sketch, "E29", {"start": v(-83, 0) * mm, "mid": v(-95, 12) * mm, "end": v(-107, 0) * mm});
            skLineSegment(sketch, "E30", {"start": v(-83, 0) * mm, "end": v(-107, 0) * mm});
            skSolve(sketch);
        }
        {
            var Q0;
            Q0 = qSketchRegion(id + "F14", true);
            var Q1;
            Q1=sQuery(id+"F14.wireOp",EDGE,"E30");
            revolve(context, id + "F15", {"operationType" : NewBodyOperationType.REMOVE, "entities" : qUnion([Q0]), "axis" : qUnion([Q1]), "revolveType" : RevolveType.FULL, "oppositeDirection" : true});
        }
        {
            var Q0;
            Q0=makeQuery(id+"F1.opExtrude","CAP_FACE",FACE,{"disambiguationData":[OSD([sQuery(id+"F0.wireOp",EDGE,"E3"),sQuery(id+"F0.wireOp",EDGE,"E4"),sQuery(id+"F0.wireOp",EDGE,"E5.MirrorCS"),sQuery(id+"F0.wireOp",EDGE,"E6.MirrorCS"),sQuery(id+"F0.wireOp",EDGE,"E8"),sQuery(id+"F0.wireOp",EDGE,"E9.1.0"),sQuery(id+"F0.wireOp",EDGE,"E9.1.1"),sQuery(id+"F0.wireOp",EDGE,"E9.1.2"),sQuery(id+"F0.wireOp",EDGE,"E9.1.3"),sQuery(id+"F0.wireOp",EDGE,"E9.2.0"),sQuery(id+"F0.wireOp",EDGE,"E9.2.1"),sQuery(id+"F0.wireOp",EDGE,"E9.2.2"),sQuery(id+"F0.wireOp",EDGE,"E9.2.3"),sQuery(id+"F0.wireOp",EDGE,"E10.3.3.0"),sQuery(id+"F0.wireOp",EDGE,"E10.5.3.0"),sQuery(id+"F0.wireOp",EDGE,"E10.6.3.0"),sQuery(id+"F0.wireOp",EDGE,"E10.9.3.0"),sQuery(id+"F0.wireOp",EDGE,"E10.3.4.0"),sQuery(id+"F0.wireOp",EDGE,"E10.5.4.0"),sQuery(id+"F0.wireOp",EDGE,"E10.6.4.0"),sQuery(id+"F0.wireOp",EDGE,"E10.9.4.0"),sQuery(id+"F0.wireOp",EDGE,"E10.3.5.0"),sQuery(id+"F0.wireOp",EDGE,"E10.5.5.0"),sQuery(id+"F0.wireOp",EDGE,"E10.6.5.0"),sQuery(id+"F0.wireOp",EDGE,"E10.9.5.0"),sQuery(id+"F0.wireOp",EDGE,"E10.3.6.0"),sQuery(id+"F0.wireOp",EDGE,"E10.5.6.0"),sQuery(id+"F0.wireOp",EDGE,"E10.6.6.0"),sQuery(id+"F0.wireOp",EDGE,"E10.9.6.0"),sQuery(id+"F0.wireOp",EDGE,"E10.3.7.0"),sQuery(id+"F0.wireOp",EDGE,"E10.5.7.0"),sQuery(id+"F0.wireOp",EDGE,"E10.6.7.0"),sQuery(id+"F0.wireOp",EDGE,"E10.9.7.0"),sQuery(id+"F0.wireOp",EDGE,"E10.3.8.0"),sQuery(id+"F0.wireOp",EDGE,"E10.5.8.0"),sQuery(id+"F0.wireOp",EDGE,"E10.6.8.0"),sQuery(id+"F0.wireOp",EDGE,"E10.9.8.0"),sQuery(id+"F0.wireOp",EDGE,"E10.3.9.0"),sQuery(id+"F0.wireOp",EDGE,"E10.5.9.0"),sQuery(id+"F0.wireOp",EDGE,"E10.6.9.0"),sQuery(id+"F0.wireOp",EDGE,"E10.9.9.0"),sQuery(id+"F0.wireOp",EDGE,"E10.3.10.0"),sQuery(id+"F0.wireOp",EDGE,"E10.5.10.0"),sQuery(id+"F0.wireOp",EDGE,"E10.6.10.0"),sQuery(id+"F0.wireOp",EDGE,"E10.9.10.0"),sQuery(id+"F0.wireOp",EDGE,"E10.3.11.0"),sQuery(id+"F0.wireOp",EDGE,"E10.5.11.0"),sQuery(id+"F0.wireOp",EDGE,"E10.6.11.0"),sQuery(id+"F0.wireOp",EDGE,"E10.9.11.0"),sQuery(id+"F0.wireOp",EDGE,"E10.3.12.0"),sQuery(id+"F0.wireOp",EDGE,"E10.5.12.0"),sQuery(id+"F0.wireOp",EDGE,"E10.6.12.0"),sQuery(id+"F0.wireOp",EDGE,"E10.9.12.0"),sQuery(id+"F0.wireOp",EDGE,"E10.3.13.0"),sQuery(id+"F0.wireOp",EDGE,"E10.5.13.0"),sQuery(id+"F0.wireOp",EDGE,"E10.6.13.0"),sQuery(id+"F0.wireOp",EDGE,"E10.9.13.0"),sQuery(id+"F0.wireOp",EDGE,"E10.3.14.0"),sQuery(id+"F0.wireOp",EDGE,"E10.5.14.0"),sQuery(id+"F0.wireOp",EDGE,"E10.6.14.0"),sQuery(id+"F0.wireOp",EDGE,"E10.9.14.0"),sQuery(id+"F0.wireOp",EDGE,"E10.3.15.0"),sQuery(id+"F0.wireOp",EDGE,"E10.5.15.0"),sQuery(id+"F0.wireOp",EDGE,"E10.6.15.0"),sQuery(id+"F0.wireOp",EDGE,"E10.9.15.0"),sQuery(id+"F0.wireOp",EDGE,"E10.3.16.0"),sQuery(id+"F0.wireOp",EDGE,"E10.5.16.0"),sQuery(id+"F0.wireOp",EDGE,"E10.6.16.0"),sQuery(id+"F0.wireOp",EDGE,"E10.9.16.0"),sQuery(id+"F0.wireOp",EDGE,"E10.3.17.0"),sQuery(id+"F0.wireOp",EDGE,"E10.5.17.0"),sQuery(id+"F0.wireOp",EDGE,"E10.6.17.0"),sQuery(id+"F0.wireOp",EDGE,"E10.9.17.0"),sQuery(id+"F0.wireOp",EDGE,"E10.3.18.0"),sQuery(id+"F0.wireOp",EDGE,"E10.5.18.0"),sQuery(id+"F0.wireOp",EDGE,"E10.6.18.0"),sQuery(id+"F0.wireOp",EDGE,"E10.9.18.0"),sQuery(id+"F0.wireOp",EDGE,"E10.3.19.0"),sQuery(id+"F0.wireOp",EDGE,"E10.5.19.0"),sQuery(id+"F0.wireOp",EDGE,"E10.6.19.0"),sQuery(id+"F0.wireOp",EDGE,"E10.9.19.0"),sQuery(id+"F0.wireOp",EDGE,"E10.3.20.0"),sQuery(id+"F0.wireOp",EDGE,"E10.5.20.0"),sQuery(id+"F0.wireOp",EDGE,"E10.6.20.0"),sQuery(id+"F0.wireOp",EDGE,"E10.9.20.0"),sQuery(id+"F0.wireOp",EDGE,"E10.3.21.0"),sQuery(id+"F0.wireOp",EDGE,"E10.5.21.0"),sQuery(id+"F0.wireOp",EDGE,"E10.6.21.0"),sQuery(id+"F0.wireOp",EDGE,"E10.9.21.0"),sQuery(id+"F0.wireOp",EDGE,"E10.3.22.0"),sQuery(id+"F0.wireOp",EDGE,"E10.5.22.0"),sQuery(id+"F0.wireOp",EDGE,"E10.6.22.0"),sQuery(id+"F0.wireOp",EDGE,"E10.9.22.0"),sQuery(id+"F0.wireOp",EDGE,"E10.3.23.0"),sQuery(id+"F0.wireOp",EDGE,"E10.5.23.0"),sQuery(id+"F0.wireOp",EDGE,"E10.6.23.0"),sQuery(id+"F0.wireOp",EDGE,"E10.9.23.0"),sQuery(id+"F0.wireOp",EDGE,"E10.3.24.0"),sQuery(id+"F0.wireOp",EDGE,"E10.5.24.0"),sQuery(id+"F0.wireOp",EDGE,"E10.6.24.0"),sQuery(id+"F0.wireOp",EDGE,"E10.9.24.0"),sQuery(id+"F0.wireOp",EDGE,"E10.3.25.0"),sQuery(id+"F0.wireOp",EDGE,"E10.5.25.0"),sQuery(id+"F0.wireOp",EDGE,"E5.MirrorCS"),sQuery(id+"F0.wireOp",EDGE,"E3"),sQuery(id+"F0.wireOp",EDGE,"E10.3.26.0"),sQuery(id+"F0.wireOp",EDGE,"E10.5.26.0"),sQuery(id+"F0.wireOp",EDGE,"E9.1.3"),sQuery(id+"F0.wireOp",EDGE,"E9.1.2"),sQuery(id+"F0.wireOp",EDGE,"E10.3.27.0"),sQuery(id+"F0.wireOp",EDGE,"E10.5.27.0"),sQuery(id+"F0.wireOp",EDGE,"E9.2.3"),sQuery(id+"F0.wireOp",EDGE,"E9.2.2"),sQuery(id+"F0.wireOp",EDGE,"E10.3.28.0"),sQuery(id+"F0.wireOp",EDGE,"E10.5.28.0"),sQuery(id+"F0.wireOp",EDGE,"E10.6.28.0"),sQuery(id+"F0.wireOp",EDGE,"E10.9.28.0"),sQuery(id+"F0.wireOp",EDGE,"E10.3.29.0"),sQuery(id+"F0.wireOp",EDGE,"E10.5.29.0"),sQuery(id+"F0.wireOp",EDGE,"E10.6.29.0"),sQuery(id+"F0.wireOp",EDGE,"E10.9.29.0"),sQuery(id+"F0.wireOp",EDGE,"E10.3.30.0"),sQuery(id+"F0.wireOp",EDGE,"E10.5.30.0"),sQuery(id+"F0.wireOp",EDGE,"E10.6.30.0"),sQuery(id+"F0.wireOp",EDGE,"E10.9.30.0"),sQuery(id+"F0.wireOp",EDGE,"E10.3.31.0"),sQuery(id+"F0.wireOp",EDGE,"E10.5.31.0"),sQuery(id+"F0.wireOp",EDGE,"E10.6.31.0"),sQuery(id+"F0.wireOp",EDGE,"E10.9.31.0"),sQuery(id+"F0.wireOp",EDGE,"E10.3.32.0"),sQuery(id+"F0.wireOp",EDGE,"E10.5.32.0"),sQuery(id+"F0.wireOp",EDGE,"E10.6.32.0"),sQuery(id+"F0.wireOp",EDGE,"E10.9.32.0"),sQuery(id+"F0.wireOp",EDGE,"E10.3.33.0"),sQuery(id+"F0.wireOp",EDGE,"E10.5.33.0"),sQuery(id+"F0.wireOp",EDGE,"E10.6.33.0"),sQuery(id+"F0.wireOp",EDGE,"E10.9.33.0"),sQuery(id+"F0.wireOp",EDGE,"E10.3.34.0"),sQuery(id+"F0.wireOp",EDGE,"E10.5.34.0"),sQuery(id+"F0.wireOp",EDGE,"E10.6.34.0"),sQuery(id+"F0.wireOp",EDGE,"E10.9.34.0"),sQuery(id+"F0.wireOp",EDGE,"E10.3.35.0"),sQuery(id+"F0.wireOp",EDGE,"E10.5.35.0"),sQuery(id+"F0.wireOp",EDGE,"E10.6.35.0"),sQuery(id+"F0.wireOp",EDGE,"E10.9.35.0"),sQuery(id+"F0.wireOp",EDGE,"E10.3.36.0"),sQuery(id+"F0.wireOp",EDGE,"E10.5.36.0"),sQuery(id+"F0.wireOp",EDGE,"E10.6.36.0"),sQuery(id+"F0.wireOp",EDGE,"E10.9.36.0"),sQuery(id+"F0.wireOp",EDGE,"E10.3.37.0"),sQuery(id+"F0.wireOp",EDGE,"E10.5.37.0"),sQuery(id+"F0.wireOp",EDGE,"E10.6.37.0"),sQuery(id+"F0.wireOp",EDGE,"E10.9.37.0"),sQuery(id+"F0.wireOp",EDGE,"E10.3.38.0"),sQuery(id+"F0.wireOp",EDGE,"E10.5.38.0"),sQuery(id+"F0.wireOp",EDGE,"E10.6.38.0"),sQuery(id+"F0.wireOp",EDGE,"E10.9.38.0"),sQuery(id+"F0.wireOp",EDGE,"E10.3.39.0"),sQuery(id+"F0.wireOp",EDGE,"E10.5.39.0"),sQuery(id+"F0.wireOp",EDGE,"E10.6.39.0"),sQuery(id+"F0.wireOp",EDGE,"E10.9.39.0"),sQuery(id+"F0.wireOp",EDGE,"E10.3.40.0"),sQuery(id+"F0.wireOp",EDGE,"E10.5.40.0"),sQuery(id+"F0.wireOp",EDGE,"E10.6.40.0"),sQuery(id+"F0.wireOp",EDGE,"E10.9.40.0"),sQuery(id+"F0.wireOp",EDGE,"E10.3.41.0"),sQuery(id+"F0.wireOp",EDGE,"E10.5.41.0"),sQuery(id+"F0.wireOp",EDGE,"E10.6.41.0"),sQuery(id+"F0.wireOp",EDGE,"E10.9.41.0"),sQuery(id+"F0.wireOp",EDGE,"E10.3.42.0"),sQuery(id+"F0.wireOp",EDGE,"E10.5.42.0"),sQuery(id+"F0.wireOp",EDGE,"E10.6.42.0"),sQuery(id+"F0.wireOp",EDGE,"E10.9.42.0"),sQuery(id+"F0.wireOp",EDGE,"E10.3.43.0"),sQuery(id+"F0.wireOp",EDGE,"E10.5.43.0"),sQuery(id+"F0.wireOp",EDGE,"E10.6.43.0"),sQuery(id+"F0.wireOp",EDGE,"E10.9.43.0"),sQuery(id+"F0.wireOp",EDGE,"E10.3.44.0"),sQuery(id+"F0.wireOp",EDGE,"E10.5.44.0"),sQuery(id+"F0.wireOp",EDGE,"E10.6.44.0"),sQuery(id+"F0.wireOp",EDGE,"E10.9.44.0"),sQuery(id+"F0.wireOp",EDGE,"E10.3.45.0"),sQuery(id+"F0.wireOp",EDGE,"E10.5.45.0"),sQuery(id+"F0.wireOp",EDGE,"E10.6.45.0"),sQuery(id+"F0.wireOp",EDGE,"E10.9.45.0"),sQuery(id+"F0.wireOp",EDGE,"E10.3.46.0"),sQuery(id+"F0.wireOp",EDGE,"E10.5.46.0"),sQuery(id+"F0.wireOp",EDGE,"E10.6.46.0"),sQuery(id+"F0.wireOp",EDGE,"E10.9.46.0"),sQuery(id+"F0.wireOp",EDGE,"E10.3.47.0"),sQuery(id+"F0.wireOp",EDGE,"E10.5.47.0"),sQuery(id+"F0.wireOp",EDGE,"E10.6.47.0"),sQuery(id+"F0.wireOp",EDGE,"E10.9.47.0"),sQuery(id+"F0.wireOp",EDGE,"E10.3.48.0"),sQuery(id+"F0.wireOp",EDGE,"E10.5.48.0"),sQuery(id+"F0.wireOp",EDGE,"E10.6.48.0"),sQuery(id+"F0.wireOp",EDGE,"E10.9.48.0"),sQuery(id+"F0.wireOp",EDGE,"E10.3.49.0"),sQuery(id+"F0.wireOp",EDGE,"E10.5.49.0"),sQuery(id+"F0.wireOp",EDGE,"E10.6.49.0"),sQuery(id+"F0.wireOp",EDGE,"E10.9.49.0")])],"isStart":true});
            var sketch = newSketch(context, id + "F16", { "sketchPlane" : qUnion([Q0])});
            skLineSegment(sketch, "E31", {"start": v(0, 0) * mm, "end": v(-67.18, 67.18) * mm, "construction": true});
            skArc(sketch, "E32", {"start": v(-58.69, 58.69) * mm, "mid": v(-58.69, 75.66) * mm, "end": v(-75.66, 75.66) * mm});
            skLineSegment(sketch, "E33", {"start": v(-58.69, 58.69) * mm, "end": v(-75.66, 75.66) * mm});
            skSolve(sketch);
        }
        {
            var Q0;
            Q0 = qSketchRegion(id + "F16", true);
            var Q1;
            Q1=sQuery(id+"F16.wireOp",EDGE,"E33");
            revolve(context, id + "F17", {"operationType" : NewBodyOperationType.REMOVE, "entities" : qUnion([Q0]), "axis" : qUnion([Q1]), "revolveType" : RevolveType.FULL, "oppositeDirection" : true});
        }
        {
            var Q0;
            Q0=makeQuery(id+"F1.opExtrude","CAP_FACE",FACE,{"disambiguationData":[OSD([sQuery(id+"F0.wireOp",EDGE,"E3"),sQuery(id+"F0.wireOp",EDGE,"E4"),sQuery(id+"F0.wireOp",EDGE,"E5.MirrorCS"),sQuery(id+"F0.wireOp",EDGE,"E6.MirrorCS"),sQuery(id+"F0.wireOp",EDGE,"E8"),sQuery(id+"F0.wireOp",EDGE,"E9.1.0"),sQuery(id+"F0.wireOp",EDGE,"E9.1.1"),sQuery(id+"F0.wireOp",EDGE,"E9.1.2"),sQuery(id+"F0.wireOp",EDGE,"E9.1.3"),sQuery(id+"F0.wireOp",EDGE,"E9.2.0"),sQuery(id+"F0.wireOp",EDGE,"E9.2.1"),sQuery(id+"F0.wireOp",EDGE,"E9.2.2"),sQuery(id+"F0.wireOp",EDGE,"E9.2.3"),sQuery(id+"F0.wireOp",EDGE,"E10.3.3.0"),sQuery(id+"F0.wireOp",EDGE,"E10.5.3.0"),sQuery(id+"F0.wireOp",EDGE,"E10.6.3.0"),sQuery(id+"F0.wireOp",EDGE,"E10.9.3.0"),sQuery(id+"F0.wireOp",EDGE,"E10.3.4.0"),sQuery(id+"F0.wireOp",EDGE,"E10.5.4.0"),sQuery(id+"F0.wireOp",EDGE,"E10.6.4.0"),sQuery(id+"F0.wireOp",EDGE,"E10.9.4.0"),sQuery(id+"F0.wireOp",EDGE,"E10.3.5.0"),sQuery(id+"F0.wireOp",EDGE,"E10.5.5.0"),sQuery(id+"F0.wireOp",EDGE,"E10.6.5.0"),sQuery(id+"F0.wireOp",EDGE,"E10.9.5.0"),sQuery(id+"F0.wireOp",EDGE,"E10.3.6.0"),sQuery(id+"F0.wireOp",EDGE,"E10.5.6.0"),sQuery(id+"F0.wireOp",EDGE,"E10.6.6.0"),sQuery(id+"F0.wireOp",EDGE,"E10.9.6.0"),sQuery(id+"F0.wireOp",EDGE,"E10.3.7.0"),sQuery(id+"F0.wireOp",EDGE,"E10.5.7.0"),sQuery(id+"F0.wireOp",EDGE,"E10.6.7.0"),sQuery(id+"F0.wireOp",EDGE,"E10.9.7.0"),sQuery(id+"F0.wireOp",EDGE,"E10.3.8.0"),sQuery(id+"F0.wireOp",EDGE,"E10.5.8.0"),sQuery(id+"F0.wireOp",EDGE,"E10.6.8.0"),sQuery(id+"F0.wireOp",EDGE,"E10.9.8.0"),sQuery(id+"F0.wireOp",EDGE,"E10.3.9.0"),sQuery(id+"F0.wireOp",EDGE,"E10.5.9.0"),sQuery(id+"F0.wireOp",EDGE,"E10.6.9.0"),sQuery(id+"F0.wireOp",EDGE,"E10.9.9.0"),sQuery(id+"F0.wireOp",EDGE,"E10.3.10.0"),sQuery(id+"F0.wireOp",EDGE,"E10.5.10.0"),sQuery(id+"F0.wireOp",EDGE,"E10.6.10.0"),sQuery(id+"F0.wireOp",EDGE,"E10.9.10.0"),sQuery(id+"F0.wireOp",EDGE,"E10.3.11.0"),sQuery(id+"F0.wireOp",EDGE,"E10.5.11.0"),sQuery(id+"F0.wireOp",EDGE,"E10.6.11.0"),sQuery(id+"F0.wireOp",EDGE,"E10.9.11.0"),sQuery(id+"F0.wireOp",EDGE,"E10.3.12.0"),sQuery(id+"F0.wireOp",EDGE,"E10.5.12.0"),sQuery(id+"F0.wireOp",EDGE,"E10.6.12.0"),sQuery(id+"F0.wireOp",EDGE,"E10.9.12.0"),sQuery(id+"F0.wireOp",EDGE,"E10.3.13.0"),sQuery(id+"F0.wireOp",EDGE,"E10.5.13.0"),sQuery(id+"F0.wireOp",EDGE,"E10.6.13.0"),sQuery(id+"F0.wireOp",EDGE,"E10.9.13.0"),sQuery(id+"F0.wireOp",EDGE,"E10.3.14.0"),sQuery(id+"F0.wireOp",EDGE,"E10.5.14.0"),sQuery(id+"F0.wireOp",EDGE,"E10.6.14.0"),sQuery(id+"F0.wireOp",EDGE,"E10.9.14.0"),sQuery(id+"F0.wireOp",EDGE,"E10.3.15.0"),sQuery(id+"F0.wireOp",EDGE,"E10.5.15.0"),sQuery(id+"F0.wireOp",EDGE,"E10.6.15.0"),sQuery(id+"F0.wireOp",EDGE,"E10.9.15.0"),sQuery(id+"F0.wireOp",EDGE,"E10.3.16.0"),sQuery(id+"F0.wireOp",EDGE,"E10.5.16.0"),sQuery(id+"F0.wireOp",EDGE,"E10.6.16.0"),sQuery(id+"F0.wireOp",EDGE,"E10.9.16.0"),sQuery(id+"F0.wireOp",EDGE,"E10.3.17.0"),sQuery(id+"F0.wireOp",EDGE,"E10.5.17.0"),sQuery(id+"F0.wireOp",EDGE,"E10.6.17.0"),sQuery(id+"F0.wireOp",EDGE,"E10.9.17.0"),sQuery(id+"F0.wireOp",EDGE,"E10.3.18.0"),sQuery(id+"F0.wireOp",EDGE,"E10.5.18.0"),sQuery(id+"F0.wireOp",EDGE,"E10.6.18.0"),sQuery(id+"F0.wireOp",EDGE,"E10.9.18.0"),sQuery(id+"F0.wireOp",EDGE,"E10.3.19.0"),sQuery(id+"F0.wireOp",EDGE,"E10.5.19.0"),sQuery(id+"F0.wireOp",EDGE,"E10.6.19.0"),sQuery(id+"F0.wireOp",EDGE,"E10.9.19.0"),sQuery(id+"F0.wireOp",EDGE,"E10.3.20.0"),sQuery(id+"F0.wireOp",EDGE,"E10.5.20.0"),sQuery(id+"F0.wireOp",EDGE,"E10.6.20.0"),sQuery(id+"F0.wireOp",EDGE,"E10.9.20.0"),sQuery(id+"F0.wireOp",EDGE,"E10.3.21.0"),sQuery(id+"F0.wireOp",EDGE,"E10.5.21.0"),sQuery(id+"F0.wireOp",EDGE,"E10.6.21.0"),sQuery(id+"F0.wireOp",EDGE,"E10.9.21.0"),sQuery(id+"F0.wireOp",EDGE,"E10.3.22.0"),sQuery(id+"F0.wireOp",EDGE,"E10.5.22.0"),sQuery(id+"F0.wireOp",EDGE,"E10.6.22.0"),sQuery(id+"F0.wireOp",EDGE,"E10.9.22.0"),sQuery(id+"F0.wireOp",EDGE,"E10.3.23.0"),sQuery(id+"F0.wireOp",EDGE,"E10.5.23.0"),sQuery(id+"F0.wireOp",EDGE,"E10.6.23.0"),sQuery(id+"F0.wireOp",EDGE,"E10.9.23.0"),sQuery(id+"F0.wireOp",EDGE,"E10.3.24.0"),sQuery(id+"F0.wireOp",EDGE,"E10.5.24.0"),sQuery(id+"F0.wireOp",EDGE,"E10.6.24.0"),sQuery(id+"F0.wireOp",EDGE,"E10.9.24.0"),sQuery(id+"F0.wireOp",EDGE,"E10.3.25.0"),sQuery(id+"F0.wireOp",EDGE,"E10.5.25.0"),sQuery(id+"F0.wireOp",EDGE,"E5.MirrorCS"),sQuery(id+"F0.wireOp",EDGE,"E3"),sQuery(id+"F0.wireOp",EDGE,"E10.3.26.0"),sQuery(id+"F0.wireOp",EDGE,"E10.5.26.0"),sQuery(id+"F0.wireOp",EDGE,"E9.1.3"),sQuery(id+"F0.wireOp",EDGE,"E9.1.2"),sQuery(id+"F0.wireOp",EDGE,"E10.3.27.0"),sQuery(id+"F0.wireOp",EDGE,"E10.5.27.0"),sQuery(id+"F0.wireOp",EDGE,"E9.2.3"),sQuery(id+"F0.wireOp",EDGE,"E9.2.2"),sQuery(id+"F0.wireOp",EDGE,"E10.3.28.0"),sQuery(id+"F0.wireOp",EDGE,"E10.5.28.0"),sQuery(id+"F0.wireOp",EDGE,"E10.6.28.0"),sQuery(id+"F0.wireOp",EDGE,"E10.9.28.0"),sQuery(id+"F0.wireOp",EDGE,"E10.3.29.0"),sQuery(id+"F0.wireOp",EDGE,"E10.5.29.0"),sQuery(id+"F0.wireOp",EDGE,"E10.6.29.0"),sQuery(id+"F0.wireOp",EDGE,"E10.9.29.0"),sQuery(id+"F0.wireOp",EDGE,"E10.3.30.0"),sQuery(id+"F0.wireOp",EDGE,"E10.5.30.0"),sQuery(id+"F0.wireOp",EDGE,"E10.6.30.0"),sQuery(id+"F0.wireOp",EDGE,"E10.9.30.0"),sQuery(id+"F0.wireOp",EDGE,"E10.3.31.0"),sQuery(id+"F0.wireOp",EDGE,"E10.5.31.0"),sQuery(id+"F0.wireOp",EDGE,"E10.6.31.0"),sQuery(id+"F0.wireOp",EDGE,"E10.9.31.0"),sQuery(id+"F0.wireOp",EDGE,"E10.3.32.0"),sQuery(id+"F0.wireOp",EDGE,"E10.5.32.0"),sQuery(id+"F0.wireOp",EDGE,"E10.6.32.0"),sQuery(id+"F0.wireOp",EDGE,"E10.9.32.0"),sQuery(id+"F0.wireOp",EDGE,"E10.3.33.0"),sQuery(id+"F0.wireOp",EDGE,"E10.5.33.0"),sQuery(id+"F0.wireOp",EDGE,"E10.6.33.0"),sQuery(id+"F0.wireOp",EDGE,"E10.9.33.0"),sQuery(id+"F0.wireOp",EDGE,"E10.3.34.0"),sQuery(id+"F0.wireOp",EDGE,"E10.5.34.0"),sQuery(id+"F0.wireOp",EDGE,"E10.6.34.0"),sQuery(id+"F0.wireOp",EDGE,"E10.9.34.0"),sQuery(id+"F0.wireOp",EDGE,"E10.3.35.0"),sQuery(id+"F0.wireOp",EDGE,"E10.5.35.0"),sQuery(id+"F0.wireOp",EDGE,"E10.6.35.0"),sQuery(id+"F0.wireOp",EDGE,"E10.9.35.0"),sQuery(id+"F0.wireOp",EDGE,"E10.3.36.0"),sQuery(id+"F0.wireOp",EDGE,"E10.5.36.0"),sQuery(id+"F0.wireOp",EDGE,"E10.6.36.0"),sQuery(id+"F0.wireOp",EDGE,"E10.9.36.0"),sQuery(id+"F0.wireOp",EDGE,"E10.3.37.0"),sQuery(id+"F0.wireOp",EDGE,"E10.5.37.0"),sQuery(id+"F0.wireOp",EDGE,"E10.6.37.0"),sQuery(id+"F0.wireOp",EDGE,"E10.9.37.0"),sQuery(id+"F0.wireOp",EDGE,"E10.3.38.0"),sQuery(id+"F0.wireOp",EDGE,"E10.5.38.0"),sQuery(id+"F0.wireOp",EDGE,"E10.6.38.0"),sQuery(id+"F0.wireOp",EDGE,"E10.9.38.0"),sQuery(id+"F0.wireOp",EDGE,"E10.3.39.0"),sQuery(id+"F0.wireOp",EDGE,"E10.5.39.0"),sQuery(id+"F0.wireOp",EDGE,"E10.6.39.0"),sQuery(id+"F0.wireOp",EDGE,"E10.9.39.0"),sQuery(id+"F0.wireOp",EDGE,"E10.3.40.0"),sQuery(id+"F0.wireOp",EDGE,"E10.5.40.0"),sQuery(id+"F0.wireOp",EDGE,"E10.6.40.0"),sQuery(id+"F0.wireOp",EDGE,"E10.9.40.0"),sQuery(id+"F0.wireOp",EDGE,"E10.3.41.0"),sQuery(id+"F0.wireOp",EDGE,"E10.5.41.0"),sQuery(id+"F0.wireOp",EDGE,"E10.6.41.0"),sQuery(id+"F0.wireOp",EDGE,"E10.9.41.0"),sQuery(id+"F0.wireOp",EDGE,"E10.3.42.0"),sQuery(id+"F0.wireOp",EDGE,"E10.5.42.0"),sQuery(id+"F0.wireOp",EDGE,"E10.6.42.0"),sQuery(id+"F0.wireOp",EDGE,"E10.9.42.0"),sQuery(id+"F0.wireOp",EDGE,"E10.3.43.0"),sQuery(id+"F0.wireOp",EDGE,"E10.5.43.0"),sQuery(id+"F0.wireOp",EDGE,"E10.6.43.0"),sQuery(id+"F0.wireOp",EDGE,"E10.9.43.0"),sQuery(id+"F0.wireOp",EDGE,"E10.3.44.0"),sQuery(id+"F0.wireOp",EDGE,"E10.5.44.0"),sQuery(id+"F0.wireOp",EDGE,"E10.6.44.0"),sQuery(id+"F0.wireOp",EDGE,"E10.9.44.0"),sQuery(id+"F0.wireOp",EDGE,"E10.3.45.0"),sQuery(id+"F0.wireOp",EDGE,"E10.5.45.0"),sQuery(id+"F0.wireOp",EDGE,"E10.6.45.0"),sQuery(id+"F0.wireOp",EDGE,"E10.9.45.0"),sQuery(id+"F0.wireOp",EDGE,"E10.3.46.0"),sQuery(id+"F0.wireOp",EDGE,"E10.5.46.0"),sQuery(id+"F0.wireOp",EDGE,"E10.6.46.0"),sQuery(id+"F0.wireOp",EDGE,"E10.9.46.0"),sQuery(id+"F0.wireOp",EDGE,"E10.3.47.0"),sQuery(id+"F0.wireOp",EDGE,"E10.5.47.0"),sQuery(id+"F0.wireOp",EDGE,"E10.6.47.0"),sQuery(id+"F0.wireOp",EDGE,"E10.9.47.0"),sQuery(id+"F0.wireOp",EDGE,"E10.3.48.0"),sQuery(id+"F0.wireOp",EDGE,"E10.5.48.0"),sQuery(id+"F0.wireOp",EDGE,"E10.6.48.0"),sQuery(id+"F0.wireOp",EDGE,"E10.9.48.0"),sQuery(id+"F0.wireOp",EDGE,"E10.3.49.0"),sQuery(id+"F0.wireOp",EDGE,"E10.5.49.0"),sQuery(id+"F0.wireOp",EDGE,"E10.6.49.0"),sQuery(id+"F0.wireOp",EDGE,"E10.9.49.0")])],"isStart":true});
            var sketch = newSketch(context, id + "F18", { "sketchPlane" : qUnion([Q0])});
            skCircle(sketch, "E34", {"center": v(0, 0) * mm, "radius": 3 * mm});
            skSolve(sketch);
        }
        {
            var Q0;
            Q0 = qSketchRegion(id + "F18", true);
            extrude(context, id + "F19", {"entities" : qUnion([Q0]), "operationType" : NewBodyOperationType.REMOVE, "oppositeDirection" : true, "depth" : 17.5 * mm});
        }
    });
